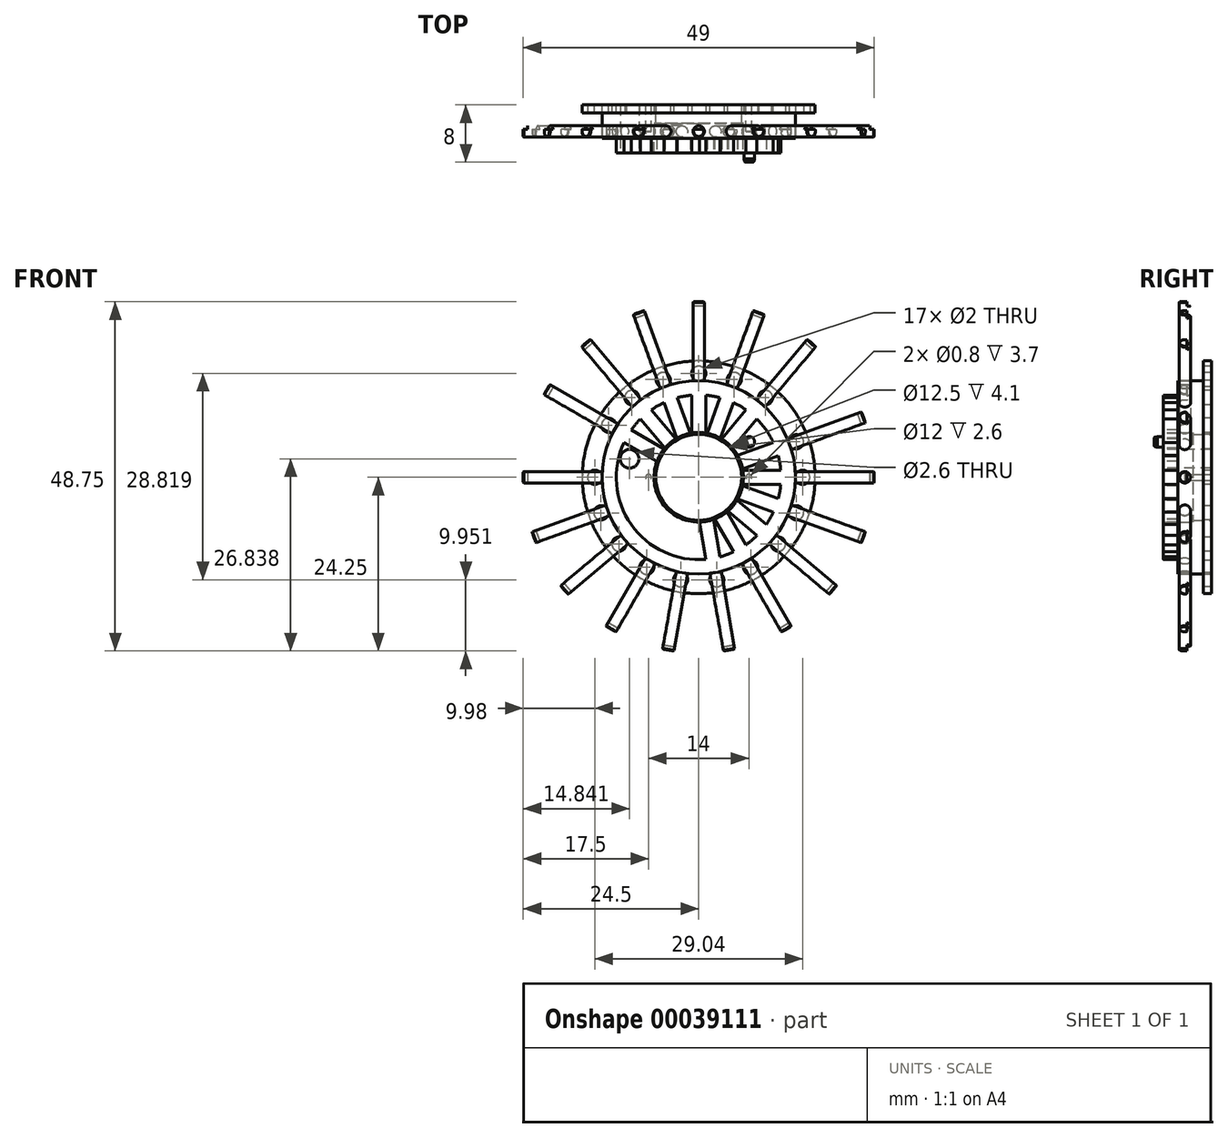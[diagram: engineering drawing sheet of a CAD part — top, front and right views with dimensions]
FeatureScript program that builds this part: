
annotation { "Feature Type Name" : "Feature", "Feature Type Description" : "" }
export const myFeature = defineFeature(function(context is Context, id is Id, definition is map)
    precondition{}
    {
        {
            var Q0;
            Q0=qCreatedBy(makeId("Right.planeOp"),FACE);
            var sketch = newSketch(context, id + "F0", { "sketchPlane" : qUnion([Q0])});
            skLineSegment(sketch, "E0", {"start": v(0, 6) * mm, "end": v(0, 16.25) * mm});
            skLineSegment(sketch, "E1", {"start": v(0, 16.25) * mm, "end": v(-1.1, 16.25) * mm});
            skLineSegment(sketch, "E2", {"start": v(-1.1, 16.25) * mm, "end": v(-1.1, 13.5) * mm});
            skLineSegment(sketch, "E3", {"start": v(-1.1, 13.5) * mm, "end": v(-4.7, 13.5) * mm});
            skLineSegment(sketch, "E4", {"start": v(-4.7, 13.5) * mm, "end": v(-4.7, 11.5) * mm});
            skLineSegment(sketch, "E5", {"start": v(-4.7, 11.5) * mm, "end": v(-6.7, 11.5) * mm});
            skLineSegment(sketch, "E6", {"start": v(-6.7, 11.5) * mm, "end": v(-6.7, 6.25) * mm});
            skLineSegment(sketch, "E7", {"start": v(0, 6) * mm, "end": v(-2.6, 6) * mm});
            skLineSegment(sketch, "E8", {"start": v(-2.6, 6) * mm, "end": v(-2.6, 6.25) * mm});
            skLineSegment(sketch, "E9", {"start": v(-2.6, 6.25) * mm, "end": v(-6.7, 6.25) * mm});
            skLineSegment(sketch, "E10", {"start": v(0, 0) * mm, "end": v(-6.75, 0) * mm, "construction": true});
            skSolve(sketch);
        }
        {
            var Q0;
            Q0=makeQuery(id+"F0.imprint","IMPRINT",FACE,{"disambiguationData":[TD([[makeQuery(id+"F0.imprint","IMPRINT",EDGE,{"derivedFrom":sQuery(id+"F0.wireOp",EDGE,"E0")}),1.0]])]});
            var Q1;
            Q1=sQuery(id+"F0.wireOp",EDGE,"E10");
            revolve(context, id + "F1", {"entities" : qUnion([Q0]), "axis" : qUnion([Q1]), "revolveType" : RevolveType.FULL});
        }
        {
            var Q0;
            Q0=makeQuery(id+"F1.opRevolve","SWEPT_FACE",FACE,{"disambiguationData":[OSD([sQuery(id+"F0.wireOp",EDGE,"E6")])]});
            var sketch = newSketch(context, id + "F2", { "sketchPlane" : qUnion([Q0])});
            skLineSegment(sketch, "E11", {"start": v(-10.42, 4.86) * mm, "end": v(-5.84, 2.22) * mm});
            skLineSegment(sketch, "E12", {"start": v(-9.42, 6.6) * mm, "end": v(-4.84, 3.95) * mm});
            skLineSegment(sketch, "E13", {"start": v(-9.96, 5.75) * mm, "end": v(0, 0) * mm, "construction": true});
            skCircle(sketch, "E14", {"center": v(0, 0) * mm, "radius": 11.5 * mm});
            skArc(sketch, "E15", {"start": v(-9.42, 6.6) * mm, "mid": v(-9.96, 5.75) * mm, "end": v(-10.42, 4.86) * mm});
            skArc(sketch, "E16", {"start": v(-4.84, 3.95) * mm, "mid": v(-5.41, 3.12) * mm, "end": v(-5.84, 2.22) * mm});
            skLineSegment(sketch, "E17.1.0", {"start": v(-6.6, 9.42) * mm, "end": v(-3.2, 5.37) * mm});
            skArc(sketch, "E17.1.1", {"start": v(-3.2, 5.37) * mm, "mid": v(-4.02, 4.79) * mm, "end": v(-4.73, 4.08) * mm});
            skLineSegment(sketch, "E17.1.2", {"start": v(-8.13, 8.13) * mm, "end": v(-4.73, 4.08) * mm});
            skArc(sketch, "E17.1.3", {"start": v(-6.6, 9.42) * mm, "mid": v(-7.4, 8.8) * mm, "end": v(-8.13, 8.13) * mm});
            skLineSegment(sketch, "E17.2.0", {"start": v(-2.98, 11.1) * mm, "end": v(-1.17, 6.14) * mm});
            skArc(sketch, "E17.2.1", {"start": v(-1.17, 6.14) * mm, "mid": v(-2.14, 5.87) * mm, "end": v(-3.05, 5.46) * mm});
            skLineSegment(sketch, "E17.2.2", {"start": v(-4.86, 10.42) * mm, "end": v(-3.05, 5.46) * mm});
            skArc(sketch, "E17.2.3", {"start": v(-2.98, 11.1) * mm, "mid": v(-3.93, 10.8) * mm, "end": v(-4.86, 10.42) * mm});
            skLineSegment(sketch, "E17.3.0", {"start": v(1, 11.46) * mm, "end": v(1, 6.17) * mm});
            skArc(sketch, "E17.3.1", {"start": v(1, 6.17) * mm, "mid": v(0, 6.25) * mm, "end": v(-1, 6.17) * mm});
            skLineSegment(sketch, "E17.3.2", {"start": v(-1, 11.46) * mm, "end": v(-1, 6.17) * mm});
            skArc(sketch, "E17.3.3", {"start": v(1, 11.46) * mm, "mid": v(0, 11.5) * mm, "end": v(-1, 11.46) * mm});
            skLineSegment(sketch, "E17.4.0", {"start": v(4.86, 10.42) * mm, "end": v(3.05, 5.46) * mm});
            skArc(sketch, "E17.4.1", {"start": v(3.05, 5.46) * mm, "mid": v(2.14, 5.87) * mm, "end": v(1.17, 6.14) * mm});
            skLineSegment(sketch, "E17.4.2", {"start": v(2.98, 11.1) * mm, "end": v(1.17, 6.14) * mm});
            skArc(sketch, "E17.4.3", {"start": v(4.86, 10.42) * mm, "mid": v(3.93, 10.8) * mm, "end": v(2.98, 11.1) * mm});
            skLineSegment(sketch, "E17.5.0", {"start": v(8.13, 8.13) * mm, "end": v(4.73, 4.08) * mm});
            skArc(sketch, "E17.5.1", {"start": v(4.73, 4.08) * mm, "mid": v(4.02, 4.79) * mm, "end": v(3.2, 5.37) * mm});
            skLineSegment(sketch, "E17.5.2", {"start": v(6.6, 9.42) * mm, "end": v(3.2, 5.37) * mm});
            skArc(sketch, "E17.5.3", {"start": v(8.13, 8.13) * mm, "mid": v(7.4, 8.8) * mm, "end": v(6.6, 9.42) * mm});
            skLineSegment(sketch, "E17.anchor1", {"start": v(0, 0) * mm, "end": v(-9.42, 6.6) * mm, "construction": true});
            skLineSegment(sketch, "E17.anchor2", {"start": v(0, 0) * mm, "end": v(8.13, 8.13) * mm, "construction": true});
            skLineSegment(sketch, "E18", {"start": v(5.46, 3.05) * mm, "end": v(10.42, 4.86) * mm});
            skLineSegment(sketch, "E19", {"start": v(11.1, 2.98) * mm, "end": v(6.14, 1.17) * mm});
            skLineSegment(sketch, "E20", {"start": v(0, 0) * mm, "end": v(10.8, 3.93) * mm, "construction": true});
            skArc(sketch, "E21", {"start": v(5.46, 3.05) * mm, "mid": v(5.87, 2.14) * mm, "end": v(6.14, 1.17) * mm});
            skArc(sketch, "E22", {"start": v(10.42, 4.86) * mm, "mid": v(10.8, 3.93) * mm, "end": v(11.1, 2.98) * mm});
            skArc(sketch, "E23", {"start": v(11.1, 2.98) * mm, "mid": v(10.8, 3.93) * mm, "end": v(10.42, 4.86) * mm});
            skArc(sketch, "E24", {"start": v(11.1, 2.98) * mm, "mid": v(11.7, 4.26) * mm, "end": v(10.42, 4.86) * mm});
            skArc(sketch, "E25.1.0", {"start": v(11.46, -1) * mm, "mid": v(12.46, 0) * mm, "end": v(11.46, 1) * mm});
            skLineSegment(sketch, "E25.1.1", {"start": v(6.17, 1) * mm, "end": v(11.46, 1) * mm});
            skArc(sketch, "E25.1.2", {"start": v(6.17, 1) * mm, "mid": v(6.25, 0) * mm, "end": v(6.17, -1) * mm});
            skLineSegment(sketch, "E25.1.3", {"start": v(11.46, -1) * mm, "end": v(6.17, -1) * mm});
            skArc(sketch, "E25.2.0", {"start": v(10.42, -4.86) * mm, "mid": v(11.7, -4.26) * mm, "end": v(11.1, -2.98) * mm});
            skLineSegment(sketch, "E25.2.1", {"start": v(6.14, -1.17) * mm, "end": v(11.1, -2.98) * mm});
            skArc(sketch, "E25.2.2", {"start": v(6.14, -1.17) * mm, "mid": v(5.87, -2.14) * mm, "end": v(5.46, -3.05) * mm});
            skLineSegment(sketch, "E25.2.3", {"start": v(10.42, -4.86) * mm, "end": v(5.46, -3.05) * mm});
            skArc(sketch, "E25.3.0", {"start": v(8.13, -8.13) * mm, "mid": v(9.54, -8) * mm, "end": v(9.42, -6.6) * mm});
            skLineSegment(sketch, "E25.3.1", {"start": v(5.37, -3.2) * mm, "end": v(9.42, -6.6) * mm});
            skArc(sketch, "E25.3.2", {"start": v(5.37, -3.2) * mm, "mid": v(4.79, -4.02) * mm, "end": v(4.08, -4.73) * mm});
            skLineSegment(sketch, "E25.3.3", {"start": v(8.13, -8.13) * mm, "end": v(4.08, -4.73) * mm});
            skArc(sketch, "E25.4.0", {"start": v(4.86, -10.42) * mm, "mid": v(6.23, -10.79) * mm, "end": v(6.6, -9.42) * mm});
            skLineSegment(sketch, "E25.4.1", {"start": v(3.95, -4.84) * mm, "end": v(6.6, -9.42) * mm});
            skArc(sketch, "E25.4.2", {"start": v(3.95, -4.84) * mm, "mid": v(3.12, -5.41) * mm, "end": v(2.22, -5.84) * mm});
            skLineSegment(sketch, "E25.4.3", {"start": v(4.86, -10.42) * mm, "end": v(2.22, -5.84) * mm});
            skArc(sketch, "E25.5.0", {"start": v(1, -11.46) * mm, "mid": v(2.16, -12.27) * mm, "end": v(2.97, -11.1) * mm});
            skLineSegment(sketch, "E25.5.1", {"start": v(2.06, -5.9) * mm, "end": v(2.97, -11.1) * mm});
            skArc(sketch, "E25.5.2", {"start": v(2.06, -5.9) * mm, "mid": v(1.09, -6.16) * mm, "end": v(0.09, -6.25) * mm});
            skLineSegment(sketch, "E25.5.3", {"start": v(1, -11.46) * mm, "end": v(0.09, -6.25) * mm});
            skCircle(sketch, "E26", {"center": v(-9.66, 2.59) * mm, "radius": 1.3 * mm});
            skLineSegment(sketch, "E27", {"start": v(-9.66, 2.59) * mm, "end": v(0, 0) * mm, "construction": true});
            skCircle(sketch, "E28", {"center": v(7.06, 4.94) * mm, "radius": 0.75 * mm});
            skLineSegment(sketch, "E29", {"start": v(7.06, 4.94) * mm, "end": v(0, 0) * mm, "construction": true});
            skSolve(sketch);
        }
        {
            var Q0;
            {var subQ0=sQuery(id+"F2.wireOp",EDGE,"E11");Q0=makeQuery(id+"F2.imprint","IMPRINT",FACE,{"disambiguationData":[TD([[makeQuery(id+"F2.imprint","IMPRINT",EDGE,{"derivedFrom":subQ0}),1.0]])]});}
            var Q1;
            {var subQ0=sQuery(id+"F2.wireOp",EDGE,"E17.1.0");Q1=makeQuery(id+"F2.imprint","IMPRINT",FACE,{"disambiguationData":[TD([[makeQuery(id+"F2.imprint","IMPRINT",EDGE,{"derivedFrom":subQ0}),-1.0]])]});}
            var Q2;
            {var subQ0=sQuery(id+"F2.wireOp",EDGE,"E17.2.0");Q2=makeQuery(id+"F2.imprint","IMPRINT",FACE,{"disambiguationData":[TD([[makeQuery(id+"F2.imprint","IMPRINT",EDGE,{"derivedFrom":subQ0}),-1.0]])]});}
            var Q3;
            {var subQ0=sQuery(id+"F2.wireOp",EDGE,"E17.3.0");Q3=makeQuery(id+"F2.imprint","IMPRINT",FACE,{"disambiguationData":[TD([[makeQuery(id+"F2.imprint","IMPRINT",EDGE,{"derivedFrom":subQ0}),-1.0]])]});}
            var Q4;
            {var subQ0=sQuery(id+"F2.wireOp",EDGE,"E17.4.0");Q4=makeQuery(id+"F2.imprint","IMPRINT",FACE,{"disambiguationData":[TD([[makeQuery(id+"F2.imprint","IMPRINT",EDGE,{"derivedFrom":subQ0}),-1.0]])]});}
            var Q5;
            {var subQ0=sQuery(id+"F2.wireOp",EDGE,"E17.5.0");Q5=makeQuery(id+"F2.imprint","IMPRINT",FACE,{"disambiguationData":[TD([[makeQuery(id+"F2.imprint","IMPRINT",EDGE,{"derivedFrom":subQ0}),-1.0]])]});}
            var Q6;
            {var subQ1=sQuery(id+"F2.wireOp",EDGE,"E18");Q6=makeQuery(id+"F2.imprint","IMPRINT",FACE,{"disambiguationData":[TD([[makeQuery(id+"F2.imprint","IMPRINT",EDGE,{"derivedFrom":subQ1}),-1.0]])]});}
            var Q7;
            {var subQ3=sQuery(id+"F2.wireOp",EDGE,"E25.1.1");Q7=makeQuery(id+"F2.imprint","IMPRINT",FACE,{"disambiguationData":[TD([[makeQuery(id+"F2.imprint","IMPRINT",EDGE,{"derivedFrom":subQ3}),-1.0]])]});}
            var Q8;
            {var subQ3=sQuery(id+"F2.wireOp",EDGE,"E25.2.1");Q8=makeQuery(id+"F2.imprint","IMPRINT",FACE,{"disambiguationData":[TD([[makeQuery(id+"F2.imprint","IMPRINT",EDGE,{"derivedFrom":subQ3}),-1.0]])]});}
            var Q9;
            {var subQ3=sQuery(id+"F2.wireOp",EDGE,"E25.3.1");Q9=makeQuery(id+"F2.imprint","IMPRINT",FACE,{"disambiguationData":[TD([[makeQuery(id+"F2.imprint","IMPRINT",EDGE,{"derivedFrom":subQ3}),-1.0]])]});}
            var Q10;
            {var subQ3=sQuery(id+"F2.wireOp",EDGE,"E25.4.1");Q10=makeQuery(id+"F2.imprint","IMPRINT",FACE,{"disambiguationData":[TD([[makeQuery(id+"F2.imprint","IMPRINT",EDGE,{"derivedFrom":subQ3}),-1.0]])]});}
            var Q11;
            {var subQ3=sQuery(id+"F2.wireOp",EDGE,"E25.5.1");Q11=makeQuery(id+"F2.imprint","IMPRINT",FACE,{"disambiguationData":[TD([[makeQuery(id+"F2.imprint","IMPRINT",EDGE,{"derivedFrom":subQ3}),-1.0]])]});}
            var Q12;
            Q12=makeQuery(id+"F1.opRevolve","SWEPT_FACE",FACE,{"disambiguationData":[OSD([sQuery(id+"F0.wireOp",EDGE,"E4")])]});
            extrude(context, id + "F3", {"entities" : qUnion([Q0, Q1, Q2, Q3, Q4, Q5, Q6, Q7, Q8, Q9, Q10, Q11]), "operationType" : NewBodyOperationType.REMOVE, "endBound" : BoundingType.UP_TO_SURFACE, "oppositeDirection" : true, "endBoundEntityFace" : qUnion([Q12]), "depth" : 25 * mm});
        }
        {
            var Q0;
            Q0=makeQuery(id+"F2.imprint","IMPRINT",FACE,{"disambiguationData":[TD([[makeQuery(id+"F2.imprint","IMPRINT",EDGE,{"derivedFrom":sQuery(id+"F2.wireOp",EDGE,"E26")}),1.0]])]});
            var Q1;
            Q1=makeQuery(id+"F1.opRevolve","SWEPT_FACE",FACE,{"disambiguationData":[OSD([sQuery(id+"F0.wireOp",EDGE,"E0")])]});
            extrude(context, id + "F4", {"entities" : qUnion([Q0]), "operationType" : NewBodyOperationType.REMOVE, "endBound" : BoundingType.UP_TO_NEXT, "oppositeDirection" : true, "endBoundEntityFace" : qUnion([Q1]), "depth" : 1.3 * mm});
        }
        {
            var Q0;
            Q0=makeQuery(id+"F2.imprint","IMPRINT",FACE,{"disambiguationData":[TD([[makeQuery(id+"F2.imprint","IMPRINT",EDGE,{"derivedFrom":sQuery(id+"F2.wireOp",EDGE,"E28")}),1.0]])]});
            var Q1;
            Q1=makeQuery(id+"F1.opRevolve","SWEPT_FACE",FACE,{"disambiguationData":[OSD([sQuery(id+"F0.wireOp",EDGE,"E0")])]});
            extrude(context, id + "F5", {"entities" : qUnion([Q0]), "operationType" : NewBodyOperationType.ADD, "endBoundEntityFace" : qUnion([Q1]), "depth" : 1.3 * mm});
        }
        {
            var Q0;
            Q0=makeQuery(id+"F3.boolean.opBoolean","SPLIT",FACE,{"disambiguationData":[TD([makeQuery(id+"F3.opExtrude","SWEPT_FACE",FACE,{"disambiguationData":[OSD([sQuery(id+"F2.wireOp",EDGE,"E11")])]})])],"derivedFrom":makeQuery(id+"F1.opRevolve","SWEPT_FACE",FACE,{"disambiguationData":[OSD([sQuery(id+"F0.wireOp",EDGE,"E6")])]})});
            cPlane(context, id + "F6", {"entities" : qUnion([Q0]), "cplaneType" : CPlaneType.OFFSET, "offset" : 3 * mm, "oppositeDirection" : true, "width" : 150 * mm, "height" : 150 * mm});
        }
        {
            var Q0;
            Q0=qCreatedBy(id+"F6.planeOp",FACE);
            var sketch = newSketch(context, id + "F7", { "sketchPlane" : qUnion([Q0])});
            skCircle(sketch, "E30.0", {"center": v(0, 0) * mm, "radius": 6 * mm});
            skCircle(sketch, "E31.0", {"center": v(0, 0) * mm, "radius": 13.5 * mm});
            skLineSegment(sketch, "E32", {"start": v(0, 0) * mm, "end": v(-11.7, 6.75) * mm, "construction": true});
            skLineSegment(sketch, "E33", {"start": v(-4.1, 3.3) * mm, "end": v(-20.82, 12.94) * mm});
            skLineSegment(sketch, "E34", {"start": v(-20.82, 12.94) * mm, "end": v(-21.22, 12.25) * mm});
            skLineSegment(sketch, "E35", {"start": v(-21.22, 12.25) * mm, "end": v(-4.5, 2.6) * mm});
            skLineSegment(sketch, "E36", {"start": v(-4.5, 2.6) * mm, "end": v(-4.1, 3.3) * mm});
            skLineSegment(sketch, "E37.1.0", {"start": v(-15.14, 19.28) * mm, "end": v(-15.75, 18.77) * mm});
            skLineSegment(sketch, "E37.1.1", {"start": v(-15.75, 18.77) * mm, "end": v(-3.34, 3.98) * mm});
            skLineSegment(sketch, "E37.1.2", {"start": v(-2.73, 4.5) * mm, "end": v(-15.14, 19.28) * mm});
            skLineSegment(sketch, "E37.1.3", {"start": v(-3.34, 3.98) * mm, "end": v(-2.73, 4.5) * mm});
            skLineSegment(sketch, "E37.2.0", {"start": v(-7.63, 23.3) * mm, "end": v(-8.38, 23.02) * mm});
            skLineSegment(sketch, "E37.2.1", {"start": v(-8.38, 23.02) * mm, "end": v(-1.78, 4.89) * mm});
            skLineSegment(sketch, "E37.2.2", {"start": v(-1.03, 5.16) * mm, "end": v(-7.63, 23.3) * mm});
            skLineSegment(sketch, "E37.2.3", {"start": v(-1.78, 4.89) * mm, "end": v(-1.03, 5.16) * mm});
            skLineSegment(sketch, "E37.3.0", {"start": v(0.8, 24.5) * mm, "end": v(0, 24.5) * mm});
            skLineSegment(sketch, "E37.3.1", {"start": v(0, 24.5) * mm, "end": v(0, 5.2) * mm});
            skLineSegment(sketch, "E37.3.2", {"start": v(0.8, 5.2) * mm, "end": v(0.8, 24.5) * mm});
            skLineSegment(sketch, "E37.3.3", {"start": v(0, 5.2) * mm, "end": v(0.8, 5.2) * mm});
            skLineSegment(sketch, "E37.4.0", {"start": v(9.13, 22.75) * mm, "end": v(8.38, 23.02) * mm});
            skLineSegment(sketch, "E37.4.1", {"start": v(8.38, 23.02) * mm, "end": v(1.78, 4.89) * mm});
            skLineSegment(sketch, "E37.4.2", {"start": v(2.53, 4.61) * mm, "end": v(9.13, 22.75) * mm});
            skLineSegment(sketch, "E37.4.3", {"start": v(1.78, 4.89) * mm, "end": v(2.53, 4.61) * mm});
            skLineSegment(sketch, "E37.5.0", {"start": v(16.36, 18.25) * mm, "end": v(15.75, 18.77) * mm});
            skLineSegment(sketch, "E37.5.1", {"start": v(15.75, 18.77) * mm, "end": v(3.34, 3.98) * mm});
            skLineSegment(sketch, "E37.5.2", {"start": v(3.96, 3.47) * mm, "end": v(16.36, 18.25) * mm});
            skLineSegment(sketch, "E37.5.3", {"start": v(3.34, 3.98) * mm, "end": v(3.96, 3.47) * mm});
            skLineSegment(sketch, "E37.anchor1", {"start": v(0, 0) * mm, "end": v(-21.22, 12.25) * mm, "construction": true});
            skLineSegment(sketch, "E37.anchor2", {"start": v(0, 0) * mm, "end": v(15.75, 18.77) * mm, "construction": true});
            skLineSegment(sketch, "E38", {"start": v(0, 0) * mm, "end": v(15.27, 5.56) * mm, "construction": true});
            skLineSegment(sketch, "E39", {"start": v(4.89, 1.78) * mm, "end": v(23.02, 8.38) * mm});
            skLineSegment(sketch, "E40", {"start": v(23.02, 8.38) * mm, "end": v(22.75, 9.13) * mm});
            skLineSegment(sketch, "E41", {"start": v(22.75, 9.13) * mm, "end": v(4.61, 2.53) * mm});
            skLineSegment(sketch, "E42", {"start": v(4.61, 2.53) * mm, "end": v(4.89, 1.78) * mm});
            skLineSegment(sketch, "E43.1.0", {"start": v(24.5, 0.8) * mm, "end": v(5.2, 0.8) * mm});
            skLineSegment(sketch, "E43.1.1", {"start": v(5.2, 0.8) * mm, "end": v(5.2, 0) * mm});
            skLineSegment(sketch, "E43.1.2", {"start": v(5.2, 0) * mm, "end": v(24.5, 0) * mm});
            skLineSegment(sketch, "E43.1.3", {"start": v(24.5, 0) * mm, "end": v(24.5, 0.8) * mm});
            skLineSegment(sketch, "E43.2.0", {"start": v(23.3, -7.63) * mm, "end": v(5.16, -1.03) * mm});
            skLineSegment(sketch, "E43.2.1", {"start": v(5.16, -1.03) * mm, "end": v(4.89, -1.78) * mm});
            skLineSegment(sketch, "E43.2.2", {"start": v(4.89, -1.78) * mm, "end": v(23.02, -8.38) * mm});
            skLineSegment(sketch, "E43.2.3", {"start": v(23.02, -8.38) * mm, "end": v(23.3, -7.63) * mm});
            skLineSegment(sketch, "E43.3.0", {"start": v(19.28, -15.14) * mm, "end": v(4.5, -2.73) * mm});
            skLineSegment(sketch, "E43.3.1", {"start": v(4.5, -2.73) * mm, "end": v(3.98, -3.34) * mm});
            skLineSegment(sketch, "E43.3.2", {"start": v(3.98, -3.34) * mm, "end": v(18.77, -15.75) * mm});
            skLineSegment(sketch, "E43.3.3", {"start": v(18.77, -15.75) * mm, "end": v(19.28, -15.14) * mm});
            skLineSegment(sketch, "E43.4.0", {"start": v(12.94, -20.82) * mm, "end": v(3.3, -4.1) * mm});
            skLineSegment(sketch, "E43.4.1", {"start": v(3.3, -4.1) * mm, "end": v(2.6, -4.5) * mm});
            skLineSegment(sketch, "E43.4.2", {"start": v(2.6, -4.5) * mm, "end": v(12.25, -21.22) * mm});
            skLineSegment(sketch, "E43.4.3", {"start": v(12.25, -21.22) * mm, "end": v(12.94, -20.82) * mm});
            skLineSegment(sketch, "E43.5.0", {"start": v(5.04, -23.99) * mm, "end": v(1.7, -4.98) * mm});
            skLineSegment(sketch, "E43.5.1", {"start": v(1.7, -4.98) * mm, "end": v(0.9, -5.12) * mm});
            skLineSegment(sketch, "E43.5.2", {"start": v(0.9, -5.12) * mm, "end": v(4.25, -24.13) * mm});
            skLineSegment(sketch, "E43.5.3", {"start": v(4.25, -24.13) * mm, "end": v(5.04, -23.99) * mm});
            skLineSegment(sketch, "E43.6.0", {"start": v(-3.47, -24.27) * mm, "end": v(-0.12, -5.26) * mm});
            skLineSegment(sketch, "E43.6.1", {"start": v(-0.12, -5.26) * mm, "end": v(-0.9, -5.12) * mm});
            skLineSegment(sketch, "E43.6.2", {"start": v(-0.9, -5.12) * mm, "end": v(-4.25, -24.13) * mm});
            skLineSegment(sketch, "E43.6.3", {"start": v(-4.25, -24.13) * mm, "end": v(-3.47, -24.27) * mm});
            skLineSegment(sketch, "E43.7.0", {"start": v(-11.56, -21.62) * mm, "end": v(-1.9, -4.9) * mm});
            skLineSegment(sketch, "E43.7.1", {"start": v(-1.9, -4.9) * mm, "end": v(-2.6, -4.5) * mm});
            skLineSegment(sketch, "E43.7.2", {"start": v(-2.6, -4.5) * mm, "end": v(-12.25, -21.22) * mm});
            skLineSegment(sketch, "E43.7.3", {"start": v(-12.25, -21.22) * mm, "end": v(-11.56, -21.62) * mm});
            skLineSegment(sketch, "E43.8.0", {"start": v(-18.25, -16.36) * mm, "end": v(-3.47, -3.96) * mm});
            skLineSegment(sketch, "E43.8.1", {"start": v(-3.47, -3.96) * mm, "end": v(-3.98, -3.34) * mm});
            skLineSegment(sketch, "E43.8.2", {"start": v(-3.98, -3.34) * mm, "end": v(-18.77, -15.75) * mm});
            skLineSegment(sketch, "E43.8.3", {"start": v(-18.77, -15.75) * mm, "end": v(-18.25, -16.36) * mm});
            skLineSegment(sketch, "E43.9.0", {"start": v(-22.75, -9.13) * mm, "end": v(-4.61, -2.53) * mm});
            skLineSegment(sketch, "E43.9.1", {"start": v(-4.61, -2.53) * mm, "end": v(-4.89, -1.78) * mm});
            skLineSegment(sketch, "E43.9.2", {"start": v(-4.89, -1.78) * mm, "end": v(-23.02, -8.38) * mm});
            skLineSegment(sketch, "E43.9.3", {"start": v(-23.02, -8.38) * mm, "end": v(-22.75, -9.13) * mm});
            skLineSegment(sketch, "E43.10.0", {"start": v(-24.5, -0.8) * mm, "end": v(-5.2, -0.8) * mm});
            skLineSegment(sketch, "E43.10.1", {"start": v(-5.2, -0.8) * mm, "end": v(-5.2, 0) * mm});
            skLineSegment(sketch, "E43.10.2", {"start": v(-5.2, 0) * mm, "end": v(-24.5, 0) * mm});
            skLineSegment(sketch, "E43.10.3", {"start": v(-24.5, 0) * mm, "end": v(-24.5, -0.8) * mm});
            skLineSegment(sketch, "E43.anchor1", {"start": v(0, 0) * mm, "end": v(4.61, 2.53) * mm, "construction": true});
            skLineSegment(sketch, "E43.anchor2", {"start": v(0, 0) * mm, "end": v(-5.2, -0.8) * mm, "construction": true});
            skSolve(sketch);
        }
        {
            var Q0;
            {var subQ5=sQuery(id+"F7.wireOp",EDGE,"E34");Q0=makeQuery(id+"F7.imprint","IMPRINT",FACE,{"disambiguationData":[TD([[makeQuery(id+"F7.imprint","IMPRINT",EDGE,{"derivedFrom":subQ5}),1.0]])]});}
            var Q1;
            Q1=sQuery(id+"F7.wireOp",EDGE,"E35");
            revolve(context, id + "F8", {"operationType" : NewBodyOperationType.ADD, "entities" : qUnion([Q0]), "axis" : qUnion([Q1]), "revolveType" : RevolveType.FULL, "oppositeDirection" : true});
        }
        {
            var Q0;
            {var subQ5=sQuery(id+"F7.wireOp",EDGE,"E37.1.0");Q0=makeQuery(id+"F7.imprint","IMPRINT",FACE,{"disambiguationData":[TD([[makeQuery(id+"F7.imprint","IMPRINT",EDGE,{"derivedFrom":subQ5}),1.0]])]});}
            var Q1;
            Q1=sQuery(id+"F7.wireOp",EDGE,"E37.1.1");
            revolve(context, id + "F9", {"operationType" : NewBodyOperationType.ADD, "entities" : qUnion([Q0]), "axis" : qUnion([Q1]), "revolveType" : RevolveType.FULL, "oppositeDirection" : true});
        }
        {
            var Q0;
            {var subQ5=sQuery(id+"F7.wireOp",EDGE,"E37.2.0");Q0=makeQuery(id+"F7.imprint","IMPRINT",FACE,{"disambiguationData":[TD([[makeQuery(id+"F7.imprint","IMPRINT",EDGE,{"derivedFrom":subQ5}),1.0]])]});}
            var Q1;
            Q1=sQuery(id+"F7.wireOp",EDGE,"E37.2.1");
            revolve(context, id + "F10", {"operationType" : NewBodyOperationType.ADD, "entities" : qUnion([Q0]), "axis" : qUnion([Q1]), "revolveType" : RevolveType.FULL, "oppositeDirection" : true});
        }
        {
            var Q0;
            {var subQ5=sQuery(id+"F7.wireOp",EDGE,"E37.3.0");Q0=makeQuery(id+"F7.imprint","IMPRINT",FACE,{"disambiguationData":[TD([[makeQuery(id+"F7.imprint","IMPRINT",EDGE,{"derivedFrom":subQ5}),1.0]])]});}
            var Q1;
            Q1=sQuery(id+"F7.wireOp",EDGE,"E37.3.1");
            revolve(context, id + "F11", {"operationType" : NewBodyOperationType.ADD, "entities" : qUnion([Q0]), "axis" : qUnion([Q1]), "revolveType" : RevolveType.FULL, "oppositeDirection" : true});
        }
        {
            var Q0;
            {var subQ5=sQuery(id+"F7.wireOp",EDGE,"E37.4.0");Q0=makeQuery(id+"F7.imprint","IMPRINT",FACE,{"disambiguationData":[TD([[makeQuery(id+"F7.imprint","IMPRINT",EDGE,{"derivedFrom":subQ5}),1.0]])]});}
            var Q1;
            Q1=sQuery(id+"F7.wireOp",EDGE,"E37.4.1");
            revolve(context, id + "F12", {"operationType" : NewBodyOperationType.ADD, "entities" : qUnion([Q0]), "axis" : qUnion([Q1]), "revolveType" : RevolveType.FULL, "oppositeDirection" : true});
        }
        {
            var Q0;
            {var subQ5=sQuery(id+"F7.wireOp",EDGE,"E37.5.0");Q0=makeQuery(id+"F7.imprint","IMPRINT",FACE,{"disambiguationData":[TD([[makeQuery(id+"F7.imprint","IMPRINT",EDGE,{"derivedFrom":subQ5}),1.0]])]});}
            var Q1;
            Q1=sQuery(id+"F7.wireOp",EDGE,"E37.5.1");
            revolve(context, id + "F13", {"operationType" : NewBodyOperationType.ADD, "entities" : qUnion([Q0]), "axis" : qUnion([Q1]), "revolveType" : RevolveType.FULL});
        }
        {
            var Q0;
            {var subQ5=sQuery(id+"F7.wireOp",EDGE,"E40");Q0=makeQuery(id+"F7.imprint","IMPRINT",FACE,{"disambiguationData":[TD([[makeQuery(id+"F7.imprint","IMPRINT",EDGE,{"derivedFrom":subQ5}),1.0]])]});}
            var Q1;
            Q1=sQuery(id+"F7.wireOp",EDGE,"E39");
            revolve(context, id + "F14", {"operationType" : NewBodyOperationType.ADD, "entities" : qUnion([Q0]), "axis" : qUnion([Q1]), "revolveType" : RevolveType.FULL, "oppositeDirection" : true});
        }
        {
            var Q0;
            {var subQ5=sQuery(id+"F7.wireOp",EDGE,"E43.1.3");Q0=makeQuery(id+"F7.imprint","IMPRINT",FACE,{"disambiguationData":[TD([[makeQuery(id+"F7.imprint","IMPRINT",EDGE,{"derivedFrom":subQ5}),1.0]])]});}
            var Q1;
            Q1=sQuery(id+"F7.wireOp",EDGE,"E43.1.2");
            revolve(context, id + "F15", {"operationType" : NewBodyOperationType.ADD, "entities" : qUnion([Q0]), "axis" : qUnion([Q1]), "revolveType" : RevolveType.FULL});
        }
        {
            var Q0;
            {var subQ5=sQuery(id+"F7.wireOp",EDGE,"E43.2.3");Q0=makeQuery(id+"F7.imprint","IMPRINT",FACE,{"disambiguationData":[TD([[makeQuery(id+"F7.imprint","IMPRINT",EDGE,{"derivedFrom":subQ5}),1.0]])]});}
            var Q1;
            Q1=sQuery(id+"F7.wireOp",EDGE,"E43.2.2");
            revolve(context, id + "F16", {"operationType" : NewBodyOperationType.ADD, "entities" : qUnion([Q0]), "axis" : qUnion([Q1]), "revolveType" : RevolveType.FULL});
        }
        {
            var Q0;
            {var subQ5=sQuery(id+"F7.wireOp",EDGE,"E43.3.3");Q0=makeQuery(id+"F7.imprint","IMPRINT",FACE,{"disambiguationData":[TD([[makeQuery(id+"F7.imprint","IMPRINT",EDGE,{"derivedFrom":subQ5}),1.0]])]});}
            var Q1;
            Q1=sQuery(id+"F7.wireOp",EDGE,"E43.3.2");
            revolve(context, id + "F17", {"operationType" : NewBodyOperationType.ADD, "entities" : qUnion([Q0]), "axis" : qUnion([Q1]), "revolveType" : RevolveType.FULL, "oppositeDirection" : true});
        }
        {
            var Q0;
            {var subQ5=sQuery(id+"F7.wireOp",EDGE,"E43.4.3");Q0=makeQuery(id+"F7.imprint","IMPRINT",FACE,{"disambiguationData":[TD([[makeQuery(id+"F7.imprint","IMPRINT",EDGE,{"derivedFrom":subQ5}),1.0]])]});}
            var Q1;
            Q1=sQuery(id+"F7.wireOp",EDGE,"E43.4.2");
            revolve(context, id + "F18", {"operationType" : NewBodyOperationType.ADD, "entities" : qUnion([Q0]), "axis" : qUnion([Q1]), "revolveType" : RevolveType.FULL, "oppositeDirection" : true});
        }
        {
            var Q0;
            {var subQ5=sQuery(id+"F7.wireOp",EDGE,"E43.4.3");Q0=makeQuery(id+"F7.imprint","IMPRINT",FACE,{"disambiguationData":[TD([[makeQuery(id+"F7.imprint","IMPRINT",EDGE,{"derivedFrom":subQ5}),1.0]])]});}
            var Q1;
            Q1=sQuery(id+"F7.wireOp",EDGE,"E43.4.2");
            revolve(context, id + "F19", {"operationType" : NewBodyOperationType.ADD, "entities" : qUnion([Q0]), "axis" : qUnion([Q1]), "revolveType" : RevolveType.FULL, "oppositeDirection" : true});
        }
        {
            var Q0;
            {var subQ5=sQuery(id+"F7.wireOp",EDGE,"E43.5.3");Q0=makeQuery(id+"F7.imprint","IMPRINT",FACE,{"disambiguationData":[TD([[makeQuery(id+"F7.imprint","IMPRINT",EDGE,{"derivedFrom":subQ5}),1.0]])]});}
            var Q1;
            Q1=sQuery(id+"F7.wireOp",EDGE,"E43.5.2");
            revolve(context, id + "F20", {"operationType" : NewBodyOperationType.ADD, "entities" : qUnion([Q0]), "axis" : qUnion([Q1]), "revolveType" : RevolveType.FULL, "oppositeDirection" : true});
        }
        {
            var Q0;
            {var subQ5=sQuery(id+"F7.wireOp",EDGE,"E43.6.3");Q0=makeQuery(id+"F7.imprint","IMPRINT",FACE,{"disambiguationData":[TD([[makeQuery(id+"F7.imprint","IMPRINT",EDGE,{"derivedFrom":subQ5}),1.0]])]});}
            var Q1;
            Q1=sQuery(id+"F7.wireOp",EDGE,"E43.6.2");
            revolve(context, id + "F21", {"operationType" : NewBodyOperationType.ADD, "entities" : qUnion([Q0]), "axis" : qUnion([Q1]), "revolveType" : RevolveType.FULL, "oppositeDirection" : true});
        }
        {
            var Q0;
            {var subQ5=sQuery(id+"F7.wireOp",EDGE,"E43.7.3");Q0=makeQuery(id+"F7.imprint","IMPRINT",FACE,{"disambiguationData":[TD([[makeQuery(id+"F7.imprint","IMPRINT",EDGE,{"derivedFrom":subQ5}),1.0]])]});}
            var Q1;
            Q1=sQuery(id+"F7.wireOp",EDGE,"E43.7.2");
            revolve(context, id + "F22", {"operationType" : NewBodyOperationType.ADD, "entities" : qUnion([Q0]), "axis" : qUnion([Q1]), "revolveType" : RevolveType.FULL});
        }
        {
            var Q0;
            {var subQ5=sQuery(id+"F7.wireOp",EDGE,"E43.8.3");Q0=makeQuery(id+"F7.imprint","IMPRINT",FACE,{"disambiguationData":[TD([[makeQuery(id+"F7.imprint","IMPRINT",EDGE,{"derivedFrom":subQ5}),1.0]])]});}
            var Q1;
            Q1=sQuery(id+"F7.wireOp",EDGE,"E43.8.2");
            revolve(context, id + "F23", {"operationType" : NewBodyOperationType.ADD, "entities" : qUnion([Q0]), "axis" : qUnion([Q1]), "revolveType" : RevolveType.FULL, "oppositeDirection" : true});
        }
        {
            var Q0;
            {var subQ5=sQuery(id+"F7.wireOp",EDGE,"E43.9.3");Q0=makeQuery(id+"F7.imprint","IMPRINT",FACE,{"disambiguationData":[TD([[makeQuery(id+"F7.imprint","IMPRINT",EDGE,{"derivedFrom":subQ5}),1.0]])]});}
            var Q1;
            Q1=sQuery(id+"F7.wireOp",EDGE,"E43.9.2");
            revolve(context, id + "F24", {"operationType" : NewBodyOperationType.ADD, "entities" : qUnion([Q0]), "axis" : qUnion([Q1]), "revolveType" : RevolveType.FULL});
        }
        {
            var Q0;
            {var subQ5=sQuery(id+"F7.wireOp",EDGE,"E43.10.3");Q0=makeQuery(id+"F7.imprint","IMPRINT",FACE,{"disambiguationData":[TD([[makeQuery(id+"F7.imprint","IMPRINT",EDGE,{"derivedFrom":subQ5}),1.0]])]});}
            var Q1;
            Q1=sQuery(id+"F7.wireOp",EDGE,"E43.10.2");
            revolve(context, id + "F25", {"operationType" : NewBodyOperationType.ADD, "entities" : qUnion([Q0]), "axis" : qUnion([Q1]), "revolveType" : RevolveType.FULL, "oppositeDirection" : true});
        }
        {
            var Q0;
            Q0=makeQuery(id+"F1.opRevolve","SWEPT_FACE",FACE,{"disambiguationData":[OSD([sQuery(id+"F0.wireOp",EDGE,"E2")])]});
            var sketch = newSketch(context, id + "F26", { "sketchPlane" : qUnion([Q0])});
            skLineSegment(sketch, "E44", {"start": v(0, 0) * mm, "end": v(-12.57, 7.26) * mm, "construction": true});
            skCircle(sketch, "E45", {"center": v(-12.57, 7.26) * mm, "radius": 1 * mm});
            skCircle(sketch, "E46.1.0", {"center": v(-9.33, 11.12) * mm, "radius": 1 * mm});
            skCircle(sketch, "E46.2.0", {"center": v(-4.97, 13.64) * mm, "radius": 1 * mm});
            skCircle(sketch, "E46.3.0", {"center": v(0, 14.52) * mm, "radius": 1 * mm});
            skCircle(sketch, "E46.4.0", {"center": v(4.97, 13.64) * mm, "radius": 1 * mm});
            skCircle(sketch, "E46.5.0", {"center": v(9.33, 11.12) * mm, "radius": 1 * mm});
            skPoint(sketch, "E46.center", {"position": v(0, 0) * mm});
            skLineSegment(sketch, "E46.anchor2", {"start": v(0, 0) * mm, "end": v(9.33, 11.12) * mm, "construction": true});
            skLineSegment(sketch, "E47", {"start": v(0, 0) * mm, "end": v(13.64, 4.97) * mm, "construction": true});
            skCircle(sketch, "E48", {"center": v(13.64, 4.97) * mm, "radius": 1 * mm});
            skCircle(sketch, "E49.1.0", {"center": v(14.52, 0) * mm, "radius": 1 * mm});
            skCircle(sketch, "E49.2.0", {"center": v(13.64, -4.97) * mm, "radius": 1 * mm});
            skCircle(sketch, "E49.3.0", {"center": v(11.12, -9.33) * mm, "radius": 1 * mm});
            skCircle(sketch, "E49.4.0", {"center": v(7.26, -12.57) * mm, "radius": 1 * mm});
            skCircle(sketch, "E49.5.0", {"center": v(2.52, -14.3) * mm, "radius": 1 * mm});
            skCircle(sketch, "E49.6.0", {"center": v(-2.52, -14.3) * mm, "radius": 1 * mm});
            skCircle(sketch, "E49.7.0", {"center": v(-7.26, -12.57) * mm, "radius": 1 * mm});
            skCircle(sketch, "E49.8.0", {"center": v(-11.12, -9.33) * mm, "radius": 1 * mm});
            skCircle(sketch, "E49.9.0", {"center": v(-13.64, -4.97) * mm, "radius": 1 * mm});
            skCircle(sketch, "E49.10.0", {"center": v(-14.52, 0) * mm, "radius": 1 * mm});
            skLineSegment(sketch, "E49.anchor2", {"start": v(0, 0) * mm, "end": v(-14.52, 0) * mm, "construction": true});
            skSolve(sketch);
        }
        {
            var Q0;
            Q0=makeQuery(id+"F26.imprint","IMPRINT",FACE,{"disambiguationData":[TD([[makeQuery(id+"F26.imprint","IMPRINT",EDGE,{"derivedFrom":sQuery(id+"F26.wireOp",EDGE,"E49.10.0")}),1.0]])]});
            var Q1;
            Q1=makeQuery(id+"F26.imprint","IMPRINT",FACE,{"disambiguationData":[TD([[makeQuery(id+"F26.imprint","IMPRINT",EDGE,{"derivedFrom":sQuery(id+"F26.wireOp",EDGE,"E45")}),1.0]])]});
            var Q2;
            Q2=makeQuery(id+"F26.imprint","IMPRINT",FACE,{"disambiguationData":[TD([[makeQuery(id+"F26.imprint","IMPRINT",EDGE,{"derivedFrom":sQuery(id+"F26.wireOp",EDGE,"E46.1.0")}),1.0]])]});
            var Q3;
            Q3=makeQuery(id+"F26.imprint","IMPRINT",FACE,{"disambiguationData":[TD([[makeQuery(id+"F26.imprint","IMPRINT",EDGE,{"derivedFrom":sQuery(id+"F26.wireOp",EDGE,"E46.2.0")}),1.0]])]});
            var Q4;
            Q4=makeQuery(id+"F26.imprint","IMPRINT",FACE,{"disambiguationData":[TD([[makeQuery(id+"F26.imprint","IMPRINT",EDGE,{"derivedFrom":sQuery(id+"F26.wireOp",EDGE,"E46.3.0")}),1.0]])]});
            var Q5;
            Q5=makeQuery(id+"F26.imprint","IMPRINT",FACE,{"disambiguationData":[TD([[makeQuery(id+"F26.imprint","IMPRINT",EDGE,{"derivedFrom":sQuery(id+"F26.wireOp",EDGE,"E46.4.0")}),1.0]])]});
            var Q6;
            Q6=makeQuery(id+"F26.imprint","IMPRINT",FACE,{"disambiguationData":[TD([[makeQuery(id+"F26.imprint","IMPRINT",EDGE,{"derivedFrom":sQuery(id+"F26.wireOp",EDGE,"E46.5.0")}),1.0]])]});
            var Q7;
            Q7=makeQuery(id+"F26.imprint","IMPRINT",FACE,{"disambiguationData":[TD([[makeQuery(id+"F26.imprint","IMPRINT",EDGE,{"derivedFrom":sQuery(id+"F26.wireOp",EDGE,"E48")}),1.0]])]});
            var Q8;
            Q8=makeQuery(id+"F26.imprint","IMPRINT",FACE,{"disambiguationData":[TD([[makeQuery(id+"F26.imprint","IMPRINT",EDGE,{"derivedFrom":sQuery(id+"F26.wireOp",EDGE,"E49.1.0")}),1.0]])]});
            var Q9;
            Q9=makeQuery(id+"F26.imprint","IMPRINT",FACE,{"disambiguationData":[TD([[makeQuery(id+"F26.imprint","IMPRINT",EDGE,{"derivedFrom":sQuery(id+"F26.wireOp",EDGE,"E49.2.0")}),1.0]])]});
            var Q10;
            Q10=makeQuery(id+"F26.imprint","IMPRINT",FACE,{"disambiguationData":[TD([[makeQuery(id+"F26.imprint","IMPRINT",EDGE,{"derivedFrom":sQuery(id+"F26.wireOp",EDGE,"E49.3.0")}),1.0]])]});
            var Q11;
            Q11=makeQuery(id+"F26.imprint","IMPRINT",FACE,{"disambiguationData":[TD([[makeQuery(id+"F26.imprint","IMPRINT",EDGE,{"derivedFrom":sQuery(id+"F26.wireOp",EDGE,"E49.4.0")}),1.0]])]});
            var Q12;
            Q12=makeQuery(id+"F26.imprint","IMPRINT",FACE,{"disambiguationData":[TD([[makeQuery(id+"F26.imprint","IMPRINT",EDGE,{"derivedFrom":sQuery(id+"F26.wireOp",EDGE,"E49.5.0")}),1.0]])]});
            var Q13;
            Q13=makeQuery(id+"F26.imprint","IMPRINT",FACE,{"disambiguationData":[TD([[makeQuery(id+"F26.imprint","IMPRINT",EDGE,{"derivedFrom":sQuery(id+"F26.wireOp",EDGE,"E49.6.0")}),1.0]])]});
            var Q14;
            Q14=makeQuery(id+"F26.imprint","IMPRINT",FACE,{"disambiguationData":[TD([[makeQuery(id+"F26.imprint","IMPRINT",EDGE,{"derivedFrom":sQuery(id+"F26.wireOp",EDGE,"E49.7.0")}),1.0]])]});
            var Q15;
            Q15=makeQuery(id+"F26.imprint","IMPRINT",FACE,{"disambiguationData":[TD([[makeQuery(id+"F26.imprint","IMPRINT",EDGE,{"derivedFrom":sQuery(id+"F26.wireOp",EDGE,"E49.8.0")}),1.0]])]});
            var Q16;
            Q16=makeQuery(id+"F26.imprint","IMPRINT",FACE,{"disambiguationData":[TD([[makeQuery(id+"F26.imprint","IMPRINT",EDGE,{"derivedFrom":sQuery(id+"F26.wireOp",EDGE,"E49.9.0")}),1.0]])]});
            var Q17;
            Q17=makeQuery(id+"F1.opRevolve","SWEPT_FACE",FACE,{"disambiguationData":[OSD([sQuery(id+"F0.wireOp",EDGE,"E0")])]});
            extrude(context, id + "F27", {"entities" : qUnion([Q0, Q1, Q2, Q3, Q4, Q5, Q6, Q7, Q8, Q9, Q10, Q11, Q12, Q13, Q14, Q15, Q16]), "operationType" : NewBodyOperationType.REMOVE, "endBound" : BoundingType.UP_TO_SURFACE, "oppositeDirection" : true, "endBoundEntityFace" : qUnion([Q17]), "depth" : 25 * mm});
        }
        {
            var Q0;
            Q0=makeQuery(id+"F1.opRevolve","SWEPT_FACE",FACE,{"disambiguationData":[OSD([sQuery(id+"F0.wireOp",EDGE,"E0")])]});
            var sketch = newSketch(context, id + "F28", { "sketchPlane" : qUnion([Q0])});
            skCircle(sketch, "E50", {"center": v(7, 0) * mm, "radius": 0.4 * mm});
            skCircle(sketch, "E51", {"center": v(-7, 0) * mm, "radius": 0.4 * mm});
            skSolve(sketch);
        }
        {
            var Q0;
            Q0=makeQuery(id+"F28.imprint","IMPRINT",FACE,{"disambiguationData":[TD([[makeQuery(id+"F28.imprint","IMPRINT",EDGE,{"derivedFrom":sQuery(id+"F28.wireOp",EDGE,"E50")}),1.0]])]});
            var Q1;
            Q1=makeQuery(id+"F28.imprint","IMPRINT",FACE,{"disambiguationData":[TD([[makeQuery(id+"F28.imprint","IMPRINT",EDGE,{"derivedFrom":sQuery(id+"F28.wireOp",EDGE,"E51")}),1.0]])]});
            extrude(context, id + "F29", {"entities" : qUnion([Q0, Q1]), "operationType" : NewBodyOperationType.REMOVE, "oppositeDirection" : true, "depth" : 3.7 * mm});
        }
        {
            var Q0;
            Q0=makeQuery(id+"F8.opRevolve","SWEPT_EDGE",EDGE,{"disambiguationData":[OSD([sQuery(id+"F7.wireOp",EDGE,"E33"),sQuery(id+"F7.wireOp",EDGE,"E34")])]});
            var Q1;
            Q1=makeQuery(id+"F9.opRevolve","SWEPT_EDGE",EDGE,{"disambiguationData":[OSD([sQuery(id+"F7.wireOp",EDGE,"E37.1.0"),sQuery(id+"F7.wireOp",EDGE,"E37.1.2")])]});
            var Q2;
            Q2=makeQuery(id+"F10.opRevolve","SWEPT_EDGE",EDGE,{"disambiguationData":[OSD([sQuery(id+"F7.wireOp",EDGE,"E37.2.0"),sQuery(id+"F7.wireOp",EDGE,"E37.2.2")])]});
            var Q3;
            Q3=makeQuery(id+"F11.opRevolve","SWEPT_EDGE",EDGE,{"disambiguationData":[OSD([sQuery(id+"F7.wireOp",EDGE,"E37.3.0"),sQuery(id+"F7.wireOp",EDGE,"E37.3.2")])]});
            var Q4;
            Q4=makeQuery(id+"F12.opRevolve","SWEPT_EDGE",EDGE,{"disambiguationData":[OSD([sQuery(id+"F7.wireOp",EDGE,"E37.4.0"),sQuery(id+"F7.wireOp",EDGE,"E37.4.2")])]});
            var Q5;
            Q5=makeQuery(id+"F13.opRevolve","SWEPT_EDGE",EDGE,{"disambiguationData":[OSD([sQuery(id+"F7.wireOp",EDGE,"E37.5.0"),sQuery(id+"F7.wireOp",EDGE,"E37.5.2")])]});
            var Q6;
            Q6=makeQuery(id+"F14.opRevolve","SWEPT_EDGE",EDGE,{"disambiguationData":[OSD([sQuery(id+"F7.wireOp",EDGE,"E40"),sQuery(id+"F7.wireOp",EDGE,"E41")])]});
            var Q7;
            Q7=makeQuery(id+"F15.opRevolve","SWEPT_EDGE",EDGE,{"disambiguationData":[OSD([sQuery(id+"F7.wireOp",EDGE,"E43.1.0"),sQuery(id+"F7.wireOp",EDGE,"E43.1.3")])]});
            var Q8;
            Q8=makeQuery(id+"F16.opRevolve","SWEPT_EDGE",EDGE,{"disambiguationData":[OSD([sQuery(id+"F7.wireOp",EDGE,"E43.2.0"),sQuery(id+"F7.wireOp",EDGE,"E43.2.3")])]});
            var Q9;
            Q9=makeQuery(id+"F17.opRevolve","SWEPT_EDGE",EDGE,{"disambiguationData":[OSD([sQuery(id+"F7.wireOp",EDGE,"E43.3.0"),sQuery(id+"F7.wireOp",EDGE,"E43.3.3")])]});
            var Q10;
            Q10=makeQuery(id+"F18.opRevolve","SWEPT_EDGE",EDGE,{"disambiguationData":[OSD([sQuery(id+"F7.wireOp",EDGE,"E43.4.0"),sQuery(id+"F7.wireOp",EDGE,"E43.4.3")])]});
            var Q11;
            Q11=makeQuery(id+"F20.opRevolve","SWEPT_EDGE",EDGE,{"disambiguationData":[OSD([sQuery(id+"F7.wireOp",EDGE,"E43.5.0"),sQuery(id+"F7.wireOp",EDGE,"E43.5.3")])]});
            var Q12;
            Q12=makeQuery(id+"F21.opRevolve","SWEPT_EDGE",EDGE,{"disambiguationData":[OSD([sQuery(id+"F7.wireOp",EDGE,"E43.6.0"),sQuery(id+"F7.wireOp",EDGE,"E43.6.3")])]});
            var Q13;
            Q13=makeQuery(id+"F22.opRevolve","SWEPT_EDGE",EDGE,{"disambiguationData":[OSD([sQuery(id+"F7.wireOp",EDGE,"E43.7.0"),sQuery(id+"F7.wireOp",EDGE,"E43.7.3")])]});
            var Q14;
            Q14=makeQuery(id+"F23.opRevolve","SWEPT_EDGE",EDGE,{"disambiguationData":[OSD([sQuery(id+"F7.wireOp",EDGE,"E43.8.0"),sQuery(id+"F7.wireOp",EDGE,"E43.8.3")])]});
            var Q15;
            Q15=makeQuery(id+"F24.opRevolve","SWEPT_EDGE",EDGE,{"disambiguationData":[OSD([sQuery(id+"F7.wireOp",EDGE,"E43.9.0"),sQuery(id+"F7.wireOp",EDGE,"E43.9.3")])]});
            var Q16;
            Q16=makeQuery(id+"F25.opRevolve","SWEPT_EDGE",EDGE,{"disambiguationData":[OSD([sQuery(id+"F7.wireOp",EDGE,"E43.10.0"),sQuery(id+"F7.wireOp",EDGE,"E43.10.3")])]});
            chamfer(context, id + "F30", {"entities" : qUnion([Q0, Q1, Q2, Q3, Q4, Q5, Q6, Q7, Q8, Q9, Q10, Q11, Q12, Q13, Q14, Q15, Q16]), "chamferType" : ChamferType.OFFSET_ANGLE, "width" : 0.1 * mm, "oppositeDirection" : false, "angle" : 45 * degree, "tangentPropagation" : true});
        }
        {
            var Q0;
            Q0=makeQuery(id+"F5.opExtrude","CAP_EDGE",EDGE,{"disambiguationData":[OSD([sQuery(id+"F2.wireOp",EDGE,"E28")])],"isStart":false});
            chamfer(context, id + "F31", {"entities" : qUnion([Q0]), "chamferType" : ChamferType.OFFSET_ANGLE, "width" : 0.1 * mm, "oppositeDirection" : false, "angle" : 78 * degree, "tangentPropagation" : true});
        }
        {
            var Q0;
            {var subQ0=sQuery(id+"F2.wireOp",EDGE,"E28");Q0=makeQuery(id+"F31.opChamfer","BLEND_EDGE",EDGE,{"blendedFrom":[makeQuery(id+"F5.opExtrude","CAP_EDGE",EDGE,{"disambiguationData":[OSD([subQ0])],"isStart":false}),makeQuery(id+"F5.opExtrude","CAP_FACE",FACE,{"disambiguationData":[OSD([subQ0])],"isStart":false})],"blendedInto":[makeQuery(id+"F5.opExtrude","CAP_FACE",FACE,{"disambiguationData":[OSD([subQ0])],"isStart":false})]});}
            fillet(context, id + "F32", {"entities" : qUnion([Q0]), "radius" : 0.2 * mm, "tangentPropagation" : true, "allowEdgeOverflow" : false});
        }
        {
            var Q0;
            Q0=makeQuery(id+"F3.boolean.opBoolean","SPLIT",FACE,{"disambiguationData":[TD([makeQuery(id+"F3.opExtrude","SWEPT_FACE",FACE,{"disambiguationData":[OSD([sQuery(id+"F2.wireOp",EDGE,"E11")])]})])],"derivedFrom":makeQuery(id+"F1.opRevolve","SWEPT_FACE",FACE,{"disambiguationData":[OSD([sQuery(id+"F0.wireOp",EDGE,"E6")])]})});
            cPlane(context, id + "F33", {"entities" : qUnion([Q0]), "cplaneType" : CPlaneType.OFFSET, "offset" : 4 * mm, "oppositeDirection" : true, "width" : 150 * mm, "height" : 150 * mm});
        }
        {
            var Q0;
            Q0=qCreatedBy(id+"F33.planeOp",FACE);
            var sketch = newSketch(context, id + "F34", { "sketchPlane" : qUnion([Q0])});
            skCircle(sketch, "E52", {"center": v(0, 0) * mm, "radius": 24.6 * mm});
            skCircle(sketch, "E53", {"center": v(0, 0) * mm, "radius": 23.9 * mm});
            skSolve(sketch);
        }
        {
            var Q0;
            Q0 = qSketchRegion(id + "F34", true);
            extrude(context, id + "F35", {"entities" : qUnion([Q0]), "operationType" : NewBodyOperationType.REMOVE, "depth" : 0.7 * mm});
        }
    });
